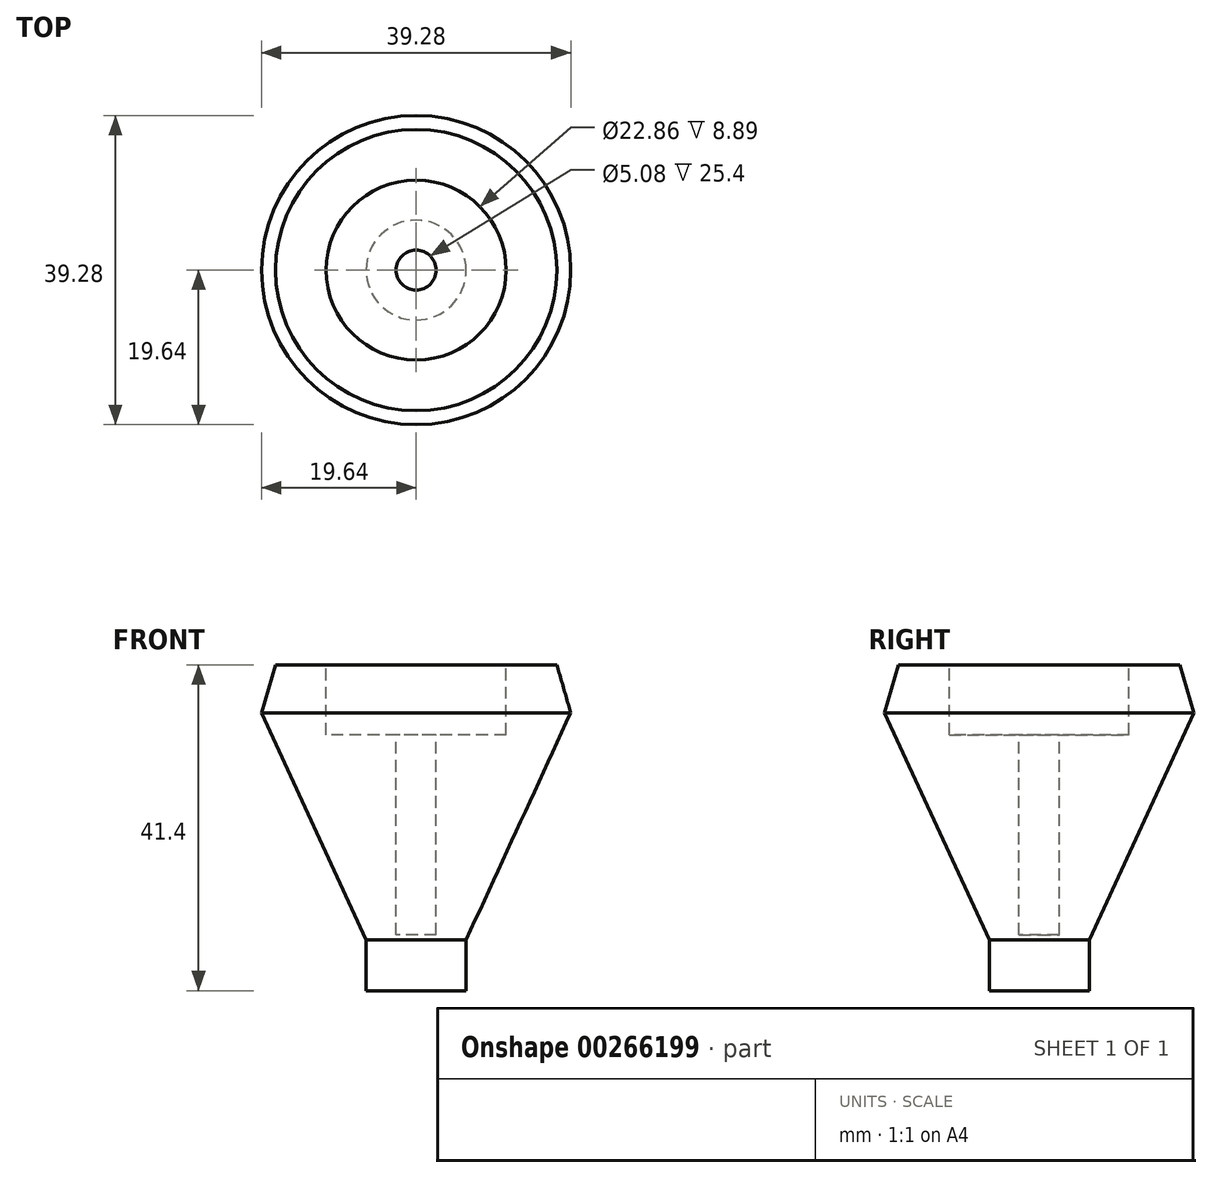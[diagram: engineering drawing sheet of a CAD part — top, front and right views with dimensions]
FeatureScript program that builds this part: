
annotation { "Feature Type Name" : "Feature", "Feature Type Description" : "" }
export const myFeature = defineFeature(function(context is Context, id is Id, definition is map)
    precondition{}
    {
        {
            var Q0;
            Q0=qCreatedBy(makeId("Front.planeOp"),FACE);
            var sketch = newSketch(context, id + "F0", { "sketchPlane" : qUnion([Q0])});
            skLineSegment(sketch, "E0", {"start": v(0, 0) * mm, "end": v(6.35, 0) * mm});
            skLineSegment(sketch, "E1", {"start": v(6.35, 0) * mm, "end": v(6.35, 6.47) * mm});
            skLineSegment(sketch, "E2", {"start": v(6.35, 6.47) * mm, "end": v(19.64, 35.3) * mm});
            skLineSegment(sketch, "E3", {"start": v(19.64, 35.3) * mm, "end": v(17.87, 41.4) * mm});
            skLineSegment(sketch, "E4", {"start": v(17.87, 41.4) * mm, "end": v(11.43, 41.4) * mm});
            skLineSegment(sketch, "E5", {"start": v(11.43, 41.4) * mm, "end": v(11.43, 32.51) * mm});
            skLineSegment(sketch, "E6", {"start": v(11.43, 32.51) * mm, "end": v(2.54, 32.51) * mm});
            skLineSegment(sketch, "E7", {"start": v(2.54, 32.51) * mm, "end": v(2.54, 7.11) * mm});
            skLineSegment(sketch, "E8", {"start": v(2.54, 7.11) * mm, "end": v(0, 7.11) * mm});
            skLineSegment(sketch, "E9", {"start": v(0, 7.11) * mm, "end": v(0, 0) * mm});
            skSolve(sketch);
        }
        {
            var Q0;
            Q0=makeQuery(id+"F0.imprint","IMPRINT",FACE,{"disambiguationData":[TD([[makeQuery(id+"F0.imprint","IMPRINT",EDGE,{"derivedFrom":sQuery(id+"F0.wireOp",EDGE,"E0")}),1.0]])]});
            var Q1;
            Q1=sQuery(id+"F0.wireOp",EDGE,"E9");
            revolve(context, id + "F1", {"entities" : qUnion([Q0]), "axis" : qUnion([Q1]), "revolveType" : RevolveType.FULL});
        }
    });
